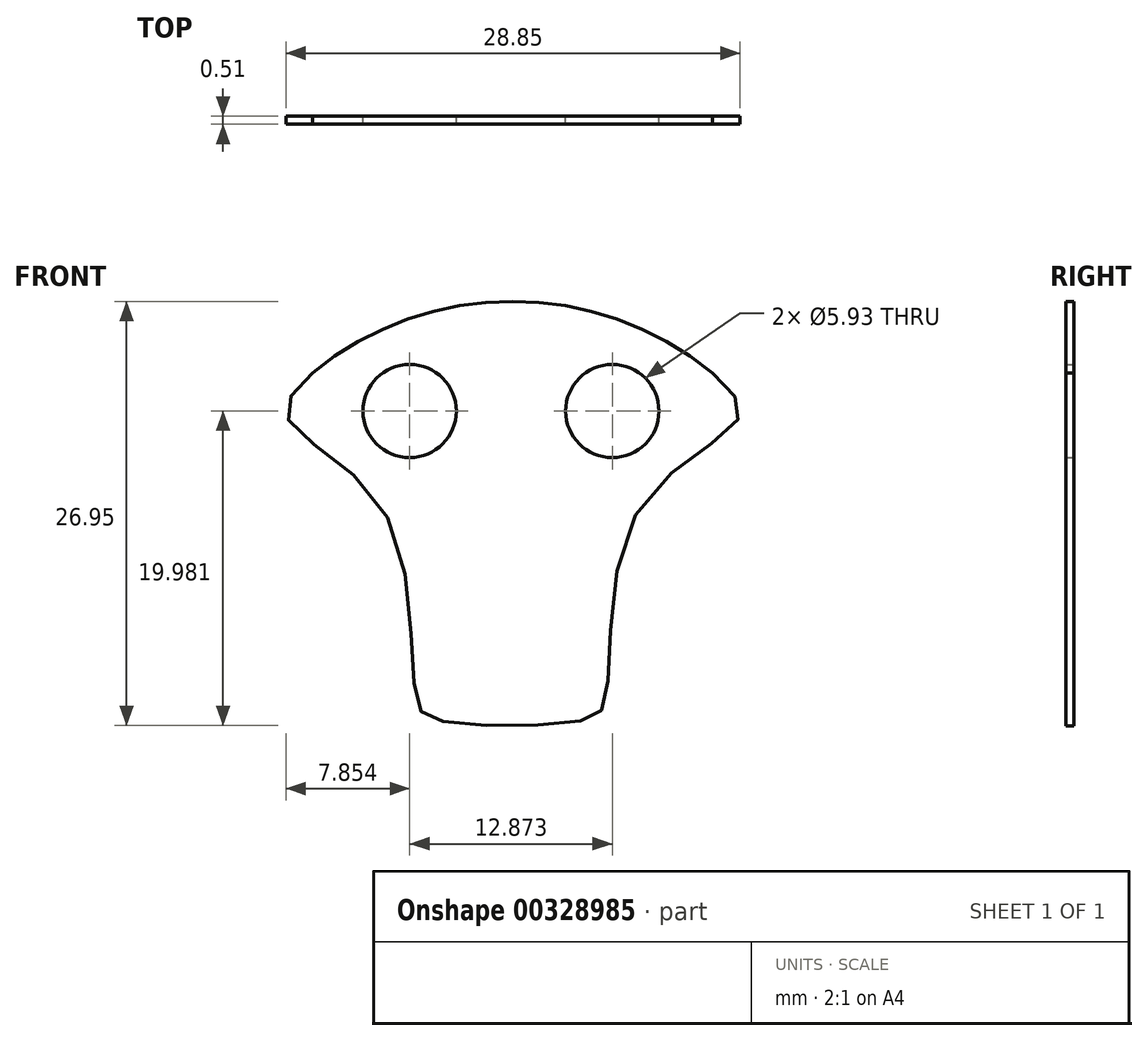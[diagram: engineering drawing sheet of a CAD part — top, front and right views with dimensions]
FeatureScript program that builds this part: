
annotation { "Feature Type Name" : "Feature", "Feature Type Description" : "" }
export const myFeature = defineFeature(function(context is Context, id is Id, definition is map)
    precondition{}
    {
        {
            var Q0;
            Q0=qCreatedBy(makeId("Front.planeOp"),FACE);
            var sketch = newSketch(context, id + "F0", { "sketchPlane" : qUnion([Q0])});
            skArc(sketch, "E0", {"start": v(12.8, 0) * mm, "mid": v(0.1, 4.55) * mm, "end": v(-12.6, 0) * mm});
            skFitSpline(sketch, "E1", {"points": [v(-12.6, 0) * mm, v(-14.23, -2.75) * mm, v(-8.1, -8.7) * mm, v(-6.04, -20.67) * mm, v(-4.42, -22.11) * mm, v(4.42, -22.11) * mm, v(6.04, -20.67) * mm, v(8.1, -8.7) * mm, v(14.5, -2.75) * mm, v(12.8, 0) * mm], "startDerivative": vector(-36.36, -30.59) * mm, "endDerivative": vector(-38.1, 34.63) * mm});
            skCircle(sketch, "E2", {"center": v(-6.44, -2.42) * mm, "radius": 2.96 * mm});
            skCircle(sketch, "E3.MirrorC", {"center": v(6.44, -2.42) * mm, "radius": 2.96 * mm});
            skSolve(sketch);
        }
        {
            var Q0;
            Q0=makeQuery(id+"F0.imprint","IMPRINT",FACE,{"disambiguationData":[TD([[makeQuery(id+"F0.imprint","IMPRINT",EDGE,{"derivedFrom":sQuery(id+"F0.wireOp",EDGE,"E0")}),1.0]])]});
            extrude(context, id + "F1", {"entities" : qUnion([Q0]), "depth" : 0.5 * mm});
        }
    });
